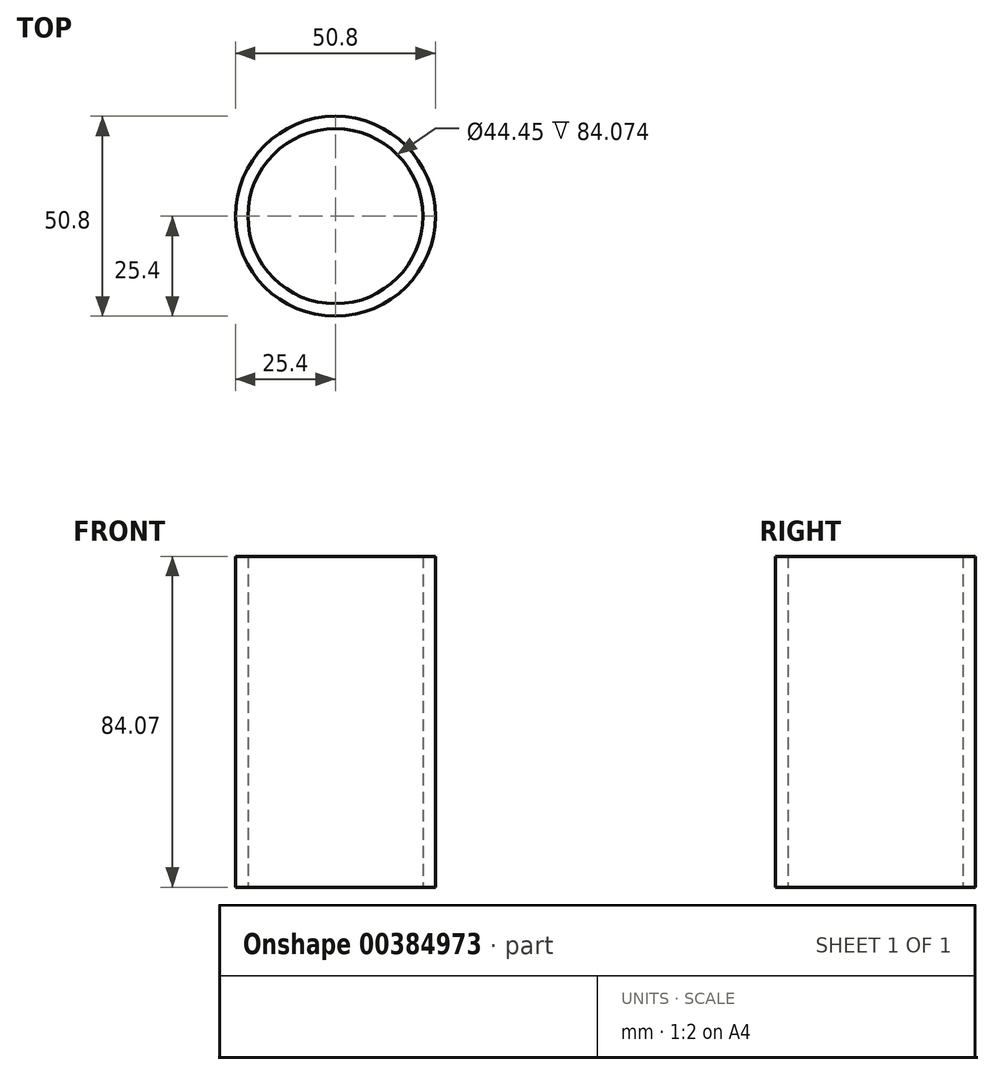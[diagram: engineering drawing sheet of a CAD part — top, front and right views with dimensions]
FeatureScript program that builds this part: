
annotation { "Feature Type Name" : "Feature", "Feature Type Description" : "" }
export const myFeature = defineFeature(function(context is Context, id is Id, definition is map)
    precondition{}
    {
        {
            var Q0;
            Q0=qCreatedBy(makeId("Top.planeOp"),FACE);
            var sketch = newSketch(context, id + "F0", { "sketchPlane" : qUnion([Q0])});
            skCircle(sketch, "E0", {"center": v(0, 0) * mm, "radius": 25.4 * mm});
            skCircle(sketch, "E1", {"center": v(0, 0) * mm, "radius": 22.22 * mm});
            skSolve(sketch);
        }
        {
            var Q0;
            Q0=makeQuery(id+"F0.imprint","IMPRINT",FACE,{"disambiguationData":[TD([[makeQuery(id+"F0.imprint","IMPRINT",EDGE,{"derivedFrom":sQuery(id+"F0.wireOp",EDGE,"E0")}),1.0]])]});
            extrude(context, id + "F1", {"entities" : qUnion([Q0]), "depth" : 84.07 * mm});
        }
    });
